# Revit family: Supply Valve
name_source: partatom
category: Air Terminals
revit_build: Autodesk Revit 2018 (Build: 20170223_1515(x64)
units: mm (PartAtom-declared; Revit-internal decimal feet)

## family parameters
Always vertical = No
Cut with Voids When Loaded = No
OmniClass Number = 23.75.00.00
OmniClass Title = Climate Control (HVAC)
Part Type = Normal
Room Calculation Point = No
Round Connector Dimension = Use Radius
Shared = No
Work Plane-Based = Yes

## types (4) — shared parameters
Default Elevation = 1219 mm
FD = No
Manufacturer = Nuaire
Pressure Drop = 0.0 Pa
SS = No
carbon = No
q-filter = Yes

## per-type parameters (varying)
| type | Description | Q | Revit Family Last Revised | Spigot Diameter | Unit Description | Weight | bezel_OD | bezel_OR | bezel_depth | bezel_width | connector_height | convex_disc | half_bezel_width | plastic | spigot_radius | steel |
| Q-AIRE-V125 | Ø125mm Q-Aire supply valve | Yes | 14/09/17 | 125 mm  [stored 0.410105 ft] | Ø125mm Q-Aire supply valve | 0.80 kg | 165 mm | 83 mm | 20 mm  [stored 0.0656168 ft] | 34 mm | 35 mm | No | 17 mm | No | 63 mm | No |
| VS150 | Ø150mm White, steel supply air valve | No | 09/04/18 | 150 mm | Ø150mm White, steel supply air valve | 0.50 kg | 180 mm  [stored 0.590551 ft] | 90 mm  [stored 0.295276 ft] | 9 mm  [stored 0.0295276 ft] | 30 mm  [stored 0.0984252 ft] | 0 mm  [stored 0 ft] | Yes | 15 mm  [stored 0.0492126 ft] | No | 75 mm | Yes |
| VS125-V | Ø125mm White, steel supply air valve | No | 14/09/17 | 125 mm  [stored 0.410105 ft] | Ø125mm White, steel supply air valve | 0.30 kg | 165 mm | 83 mm | 9 mm  [stored 0.0295276 ft] | 30 mm  [stored 0.0984252 ft] | 0 mm  [stored 0 ft] | Yes | 15 mm  [stored 0.0492126 ft] | No | 63 mm | Yes |
| V125 | Ø125mm Plastic supply air valve | No | 14/09/17 | 125 mm  [stored 0.410105 ft] | Ø125mm Plastic supply air valve | 0.20 kg | 165 mm | 83 mm | 20 mm  [stored 0.0656168 ft] | 34 mm | 0 mm  [stored 0 ft] | No | 17 mm | Yes | 63 mm | No |

note: column(s) folded — value = type name in every type: Model, Nuaire Model No, Supplier Part No

note: [stored X ft] marks values corroborated as IEEE doubles in the binary element streams (Revit-internal decimal feet)

## geometry (parser evidence)
native form markers: Blend x16, Sweep x11
no freeform markers — native parametric forms only
